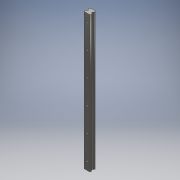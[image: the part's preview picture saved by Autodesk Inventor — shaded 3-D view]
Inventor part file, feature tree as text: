
AUTODESK INVENTOR PART (.ipt)
format: ipt  version: 2016 (Build 200138000, 138)  size: 202,240 bytes
history: native  units: mm
features: sketch x2, other x1, extrude x1, hole x1, projected_geometry x1
ambient origin geometry x8: Origin, YZ Plane, XZ Plane, XY Plane, X Axis, Y Axis, Z Axis, Center Point
bodies: Body1 (feature_tree)
feature tree (6):
  other  "РабПлоскость1"
  extrude  "Выдавливание1"  Depth=340.0mm TaperAngle=0.0deg
  hole  "Отверстие1"  [1 undecoded]
  sketch  "Эскиз2"
  projected_geometry  "Спроецированная петля1"
  sketch  "Эскиз3"
note: 1 required parameter value undecoded (feature->parameter linkage not recoverable at this tier; creation-order binding heuristic only, values carry confidence <= 0.55)
